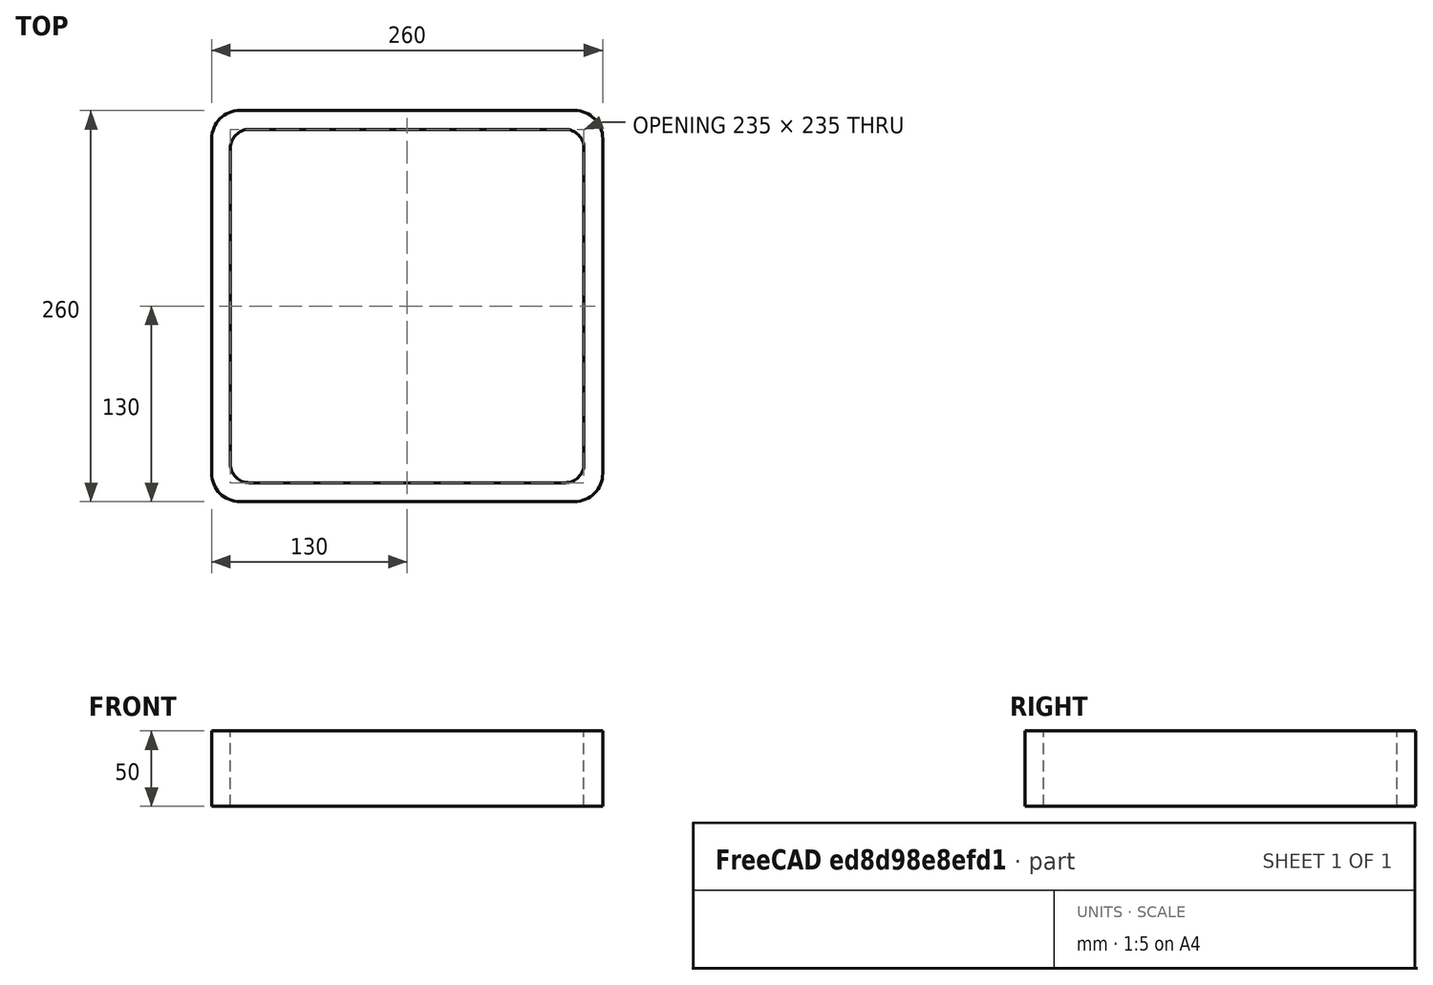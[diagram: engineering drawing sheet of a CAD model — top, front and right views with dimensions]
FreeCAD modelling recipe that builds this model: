
FCSTD DOCUMENT  (FreeCAD 0.15R4671 (Git))
Label: Square hollow section 260x260x12.5 EN10219 S235JRH
License: All rights reserved
LicenseURL: http://en.wikipedia.org/wiki/All_rights_reserved
objects: Sketcher::SketchObject×1, Part::Extrusion×1
note: 2 computed .brp shape members not serialized (recipe doc carries the construction recipe); baked Part::Feature solids carry a one-line shape summary decoded from their .brp

FEATURE [Sketcher::SketchObject] Sketch
  sketch-geometry (16):
    g0: LineSegment StartX=-105 StartY=117.5 StartZ=0 EndX=105 EndY=117.5 EndZ=0
    g1: LineSegment StartX=117.5 StartY=105 StartZ=0 EndX=117.5 EndY=-105 EndZ=0
    g2: LineSegment StartX=105 StartY=-117.5 StartZ=0 EndX=-105 EndY=-117.5 EndZ=0
    g3: LineSegment StartX=-117.5 StartY=-105 StartZ=0 EndX=-117.5 EndY=105 EndZ=0
    g4: LineSegment StartX=-111.25 StartY=130 StartZ=0 EndX=111.25 EndY=130 EndZ=0
    g5: LineSegment StartX=130 StartY=111.25 StartZ=0 EndX=130 EndY=-111.25 EndZ=0
    g6: LineSegment StartX=111.25 StartY=-130 StartZ=0 EndX=-111.25 EndY=-130 EndZ=0
    g7: LineSegment StartX=-130 StartY=-111.25 StartZ=0 EndX=-130 EndY=111.25 EndZ=0
    g8: ArcOfCircle CenterX=-105 CenterY=105 CenterZ=0 NormalX=0 NormalY=0 NormalZ=1 Radius=12.5 StartAngle=1.5708 EndAngle=3.14159
    g9: ArcOfCircle CenterX=105 CenterY=105 CenterZ=0 NormalX=0 NormalY=0 NormalZ=1 Radius=12.5 StartAngle=0 EndAngle=1.5708
    g10: ArcOfCircle CenterX=105 CenterY=-105 CenterZ=0 NormalX=0 NormalY=0 NormalZ=1 Radius=12.5 StartAngle=4.71239 EndAngle=6.28319
    g11: ArcOfCircle CenterX=-105 CenterY=-105 CenterZ=0 NormalX=0 NormalY=0 NormalZ=1 Radius=12.5 StartAngle=3.14159 EndAngle=4.71239
    g12: ArcOfCircle CenterX=111.25 CenterY=111.25 CenterZ=0 NormalX=0 NormalY=0 NormalZ=1 Radius=18.75 StartAngle=0 EndAngle=1.5708
    g13: ArcOfCircle CenterX=111.25 CenterY=-111.25 CenterZ=0 NormalX=0 NormalY=0 NormalZ=1 Radius=18.75 StartAngle=4.71239 EndAngle=6.28319
    g14: ArcOfCircle CenterX=-111.25 CenterY=-111.25 CenterZ=0 NormalX=0 NormalY=0 NormalZ=1 Radius=18.75 StartAngle=3.14159 EndAngle=4.71239
    g15: ArcOfCircle CenterX=-111.25 CenterY=111.25 CenterZ=0 NormalX=0 NormalY=0 NormalZ=1 Radius=18.75 StartAngle=1.5708 EndAngle=3.14159
  constraints (36):
    c: Horizontal(g2)
    c: Vertical(g3)
    c: Horizontal(g6)
    c: Vertical(g7)
    c: Tangent(g3,g8) = 1.5708
    c: Tangent(g0,g8) = 1.5708
    c: Tangent(g0,g9) = 1.5708
    c: Tangent(g1,g9) = 1.5708
    c: Tangent(g1,g10) = 1.5708
    c: Tangent(g2,g10) = 1.5708
    c: Tangent(g2,g11) = 1.5708
    c: Tangent(g3,g11) = 1.5708
    c: Tangent(g4,g12) = 1.5708
    c: Tangent(g5,g12) = 1.5708
    c: Tangent(g5,g13) = 1.5708
    c: Tangent(g6,g13) = 1.5708
    c: Tangent(g6,g14) = 1.5708
    c: Tangent(g7,g14) = 1.5708
    c: Tangent(g7,g15) = 1.5708
    c: Tangent(g4,g15) = 1.5708
    c: Equal(g9,g8)
    c: Equal(g9,g11)
    c: Equal(g9,g10)
    c: Equal(g12,g15)
    c: Equal(g12,g14)
    c: Equal(g12,g13)
    c: Symmetric(g4,g6,g-1)
    c: Symmetric(g7,g5,g-2)
    c: DistanceY(g4,g6) = -260
    c: DistanceX(g7,g5) = 260
    c: Symmetric(g3,g1,g-2)
    c: Symmetric(g0,g2,g-1)
    c: DistanceY(g0,g4) = 12.5
    c: DistanceX(g5,g1) = -12.5
    c: Radius(g9) = 12.5
    c: Radius(g12) = 18.75
FEATURE [Part::Extrusion] Extrude  label="Square hollow section 260x260x12.5 EN10219 S235JRH"
  Base = -> Sketch
  Dir = (0,0,50)
  Solid = true
